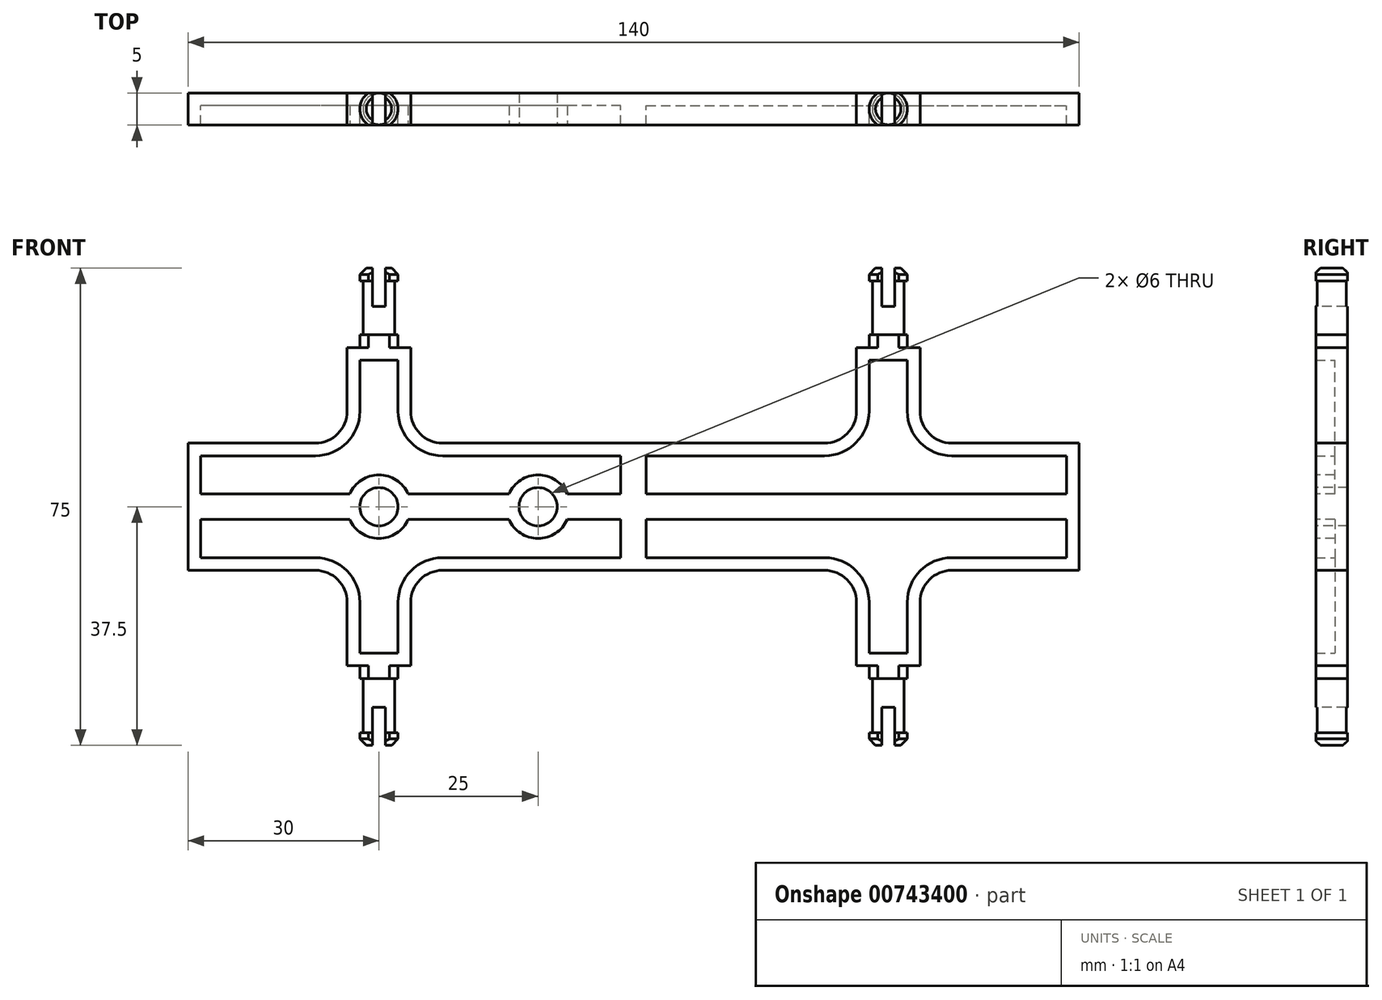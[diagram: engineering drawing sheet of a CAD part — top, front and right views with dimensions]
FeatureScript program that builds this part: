
annotation { "Feature Type Name" : "Feature", "Feature Type Description" : "" }
export const myFeature = defineFeature(function(context is Context, id is Id, definition is map)
    precondition{}
    {
        {
            var Q0;
            Q0=qCreatedBy(makeId("Front.planeOp"),FACE);
            var sketch = newSketch(context, id + "F0", { "sketchPlane" : qUnion([Q0])});
            skLineSegment(sketch, "E0.bottom", {"start": v(0, 0) * mm, "end": v(70, 0) * mm});
            skLineSegment(sketch, "E0.top", {"start": v(0, 10) * mm, "end": v(30, 10) * mm});
            skLineSegment(sketch, "E0.left", {"start": v(0, 0) * mm, "end": v(0, 10) * mm});
            skLineSegment(sketch, "E0.right", {"start": v(70, 0) * mm, "end": v(70, 10) * mm});
            skLineSegment(sketch, "E1.top", {"start": v(35, 25) * mm, "end": v(45, 25) * mm});
            skLineSegment(sketch, "E1.left", {"start": v(35, 15) * mm, "end": v(35, 25) * mm});
            skLineSegment(sketch, "E1.right", {"start": v(45, 15) * mm, "end": v(45, 25) * mm});
            skLineSegment(sketch, "E2.trimOffspring", {"start": v(50, 10) * mm, "end": v(70, 10) * mm});
            skPoint(sketch, "E3.visualSharp", {"position": v(35, 10) * mm});
            skArc(sketch, "E3.filletArc", {"start": v(30, 10) * mm, "mid": v(33.54, 11.46) * mm, "end": v(35, 15) * mm});
            skPoint(sketch, "E4.visualSharp", {"position": v(45, 10) * mm});
            skArc(sketch, "E4.filletArc", {"start": v(45, 15) * mm, "mid": v(46.46, 11.46) * mm, "end": v(50, 10) * mm});
            skSolve(sketch);
        }
        {
            var Q0;
            Q0 = qSketchRegion(id + "F0", true);
            extrude(context, id + "F1", {"entities" : qUnion([Q0]), "endBound" : BoundingType.SYMMETRIC, "depth" : 5 * mm, "offsetDistance" : 25 * mm});
        }
        {
            var Q0;
            Q0=makeQuery(id+"F1.opExtrude","CAP_FACE",FACE,{"disambiguationData":[OSD([sQuery(id+"F0.wireOp",EDGE,"E0.bottom"),sQuery(id+"F0.wireOp",EDGE,"E0.top"),sQuery(id+"F0.wireOp",EDGE,"E0.left"),sQuery(id+"F0.wireOp",EDGE,"E0.right"),sQuery(id+"F0.wireOp",EDGE,"E1.top"),sQuery(id+"F0.wireOp",EDGE,"E1.left"),sQuery(id+"F0.wireOp",EDGE,"E1.right"),sQuery(id+"F0.wireOp",EDGE,"E2.trimOffspring"),sQuery(id+"F0.wireOp",EDGE,"E3.filletArc"),sQuery(id+"F0.wireOp",EDGE,"E4.filletArc")])],"isStart":false});
            shell(context, id + "F2", {"entities" : qUnion([Q0]), "thickness" : 2 * mm});
        }
        {
            var Q0;
            Q0=qCreatedBy(makeId("Front.planeOp"),FACE);
            var sketch = newSketch(context, id + "F3", { "sketchPlane" : qUnion([Q0])});
            skLineSegment(sketch, "E5", {"start": v(40, 25) * mm, "end": v(40, 37.5) * mm});
            skLineSegment(sketch, "E6", {"start": v(40, 37.5) * mm, "end": v(37, 37.5) * mm});
            skLineSegment(sketch, "E7", {"start": v(37, 37.5) * mm, "end": v(37, 35.5) * mm});
            skLineSegment(sketch, "E8", {"start": v(37, 35.5) * mm, "end": v(37.5, 35.5) * mm});
            skLineSegment(sketch, "E9", {"start": v(37.5, 35.5) * mm, "end": v(37.5, 27) * mm});
            skLineSegment(sketch, "E10", {"start": v(37.5, 27) * mm, "end": v(37, 27) * mm});
            skLineSegment(sketch, "E11", {"start": v(37, 27) * mm, "end": v(37, 25) * mm});
            skLineSegment(sketch, "E12", {"start": v(37, 25) * mm, "end": v(40, 25) * mm});
            skSolve(sketch);
        }
        {
            var Q0;
            Q0 = qSketchRegion(id + "F3", true);
            var Q1;
            Q1=sQuery(id+"F3.wireOp",EDGE,"E5");
            revolve(context, id + "F4", {"operationType" : NewBodyOperationType.ADD, "surfaceOperationType" : NewSurfaceOperationType.NEW, "entities" : qUnion([Q0]), "axis" : qUnion([Q1]), "revolveType" : RevolveType.FULL});
        }
        {
            var Q0;
            Q0=makeQuery(id+"F4.opRevolve","SWEPT_FACE",FACE,{"disambiguationData":[OSD([sQuery(id+"F3.wireOp",EDGE,"E6")])]});
            chamfer(context, id + "F5", {"entities" : qUnion([Q0]), "width" : 1 * mm, "tangentPropagation" : true});
        }
        {
            var Q0;
            Q0=makeQuery(id+"F4.opRevolve","SWEPT_FACE",FACE,{"disambiguationData":[OSD([sQuery(id+"F3.wireOp",EDGE,"E6")])]});
            var sketch = newSketch(context, id + "F6", { "sketchPlane" : qUnion([Q0])});
            skLineSegment(sketch, "E13.bottom", {"start": v(0, 2.5) * mm, "end": v(75, 2.5) * mm});
            skLineSegment(sketch, "E13.top", {"start": v(0, -2.5) * mm, "end": v(75, -2.5) * mm});
            skLineSegment(sketch, "E13.left", {"start": v(0, 2.5) * mm, "end": v(0, -2.5) * mm});
            skLineSegment(sketch, "E13.right", {"start": v(75, 2.5) * mm, "end": v(75, -2.5) * mm});
            skSolve(sketch);
        }
        {
            var Q0;
            Q0 = qSketchRegion(id + "F6", true);
            extrude(context, id + "F7", {"entities" : qUnion([Q0]), "operationType" : NewBodyOperationType.INTERSECT, "endBound" : BoundingType.THROUGH_ALL, "oppositeDirection" : true, "depth" : 25 * mm, "offsetDistance" : 25 * mm});
        }
        {
            var Q0;
            Q0=makeQuery(id+"F4.opRevolve","SWEPT_FACE",FACE,{"disambiguationData":[OSD([sQuery(id+"F3.wireOp",EDGE,"E6")])]});
            var sketch = newSketch(context, id + "F8", { "sketchPlane" : qUnion([Q0])});
            skLineSegment(sketch, "E14.bottom", {"start": v(39, 4.04) * mm, "end": v(41, 4.04) * mm});
            skLineSegment(sketch, "E14.top", {"start": v(39, -3.46) * mm, "end": v(41, -3.46) * mm});
            skLineSegment(sketch, "E14.left", {"start": v(39, 4.04) * mm, "end": v(39, -3.46) * mm});
            skLineSegment(sketch, "E14.right", {"start": v(41, 4.04) * mm, "end": v(41, -3.46) * mm});
            skSolve(sketch);
        }
        {
            var Q0;
            Q0 = qSketchRegion(id + "F8", true);
            extrude(context, id + "F9", {"entities" : qUnion([Q0]), "operationType" : NewBodyOperationType.REMOVE, "oppositeDirection" : true, "depth" : 6 * mm, "offsetDistance" : 25 * mm});
        }
        {
            var Q0;
            Q0=makeQuery(id+"F1.opExtrude","SWEPT_BODY",BODY,{"disambiguationData":[OSD([sQuery(id+"F0.wireOp",EDGE,"E0.bottom"),sQuery(id+"F0.wireOp",EDGE,"E0.top"),sQuery(id+"F0.wireOp",EDGE,"E0.left"),sQuery(id+"F0.wireOp",EDGE,"E0.right"),sQuery(id+"F0.wireOp",EDGE,"E1.top"),sQuery(id+"F0.wireOp",EDGE,"E1.left"),sQuery(id+"F0.wireOp",EDGE,"E1.right"),sQuery(id+"F0.wireOp",EDGE,"E2.trimOffspring"),sQuery(id+"F0.wireOp",EDGE,"E3.filletArc"),sQuery(id+"F0.wireOp",EDGE,"E4.filletArc")])]});
            var Q1;
            Q1=qCreatedBy(makeId("Top.planeOp"),FACE);
            mirror(context, id + "F10", {"operationType" : NewBodyOperationType.ADD, "entities" : qUnion([Q0]), "mirrorPlane" : qUnion([Q1])});
        }
        {
            var Q0;
            Q0=makeQuery(id+"F1.opExtrude","SWEPT_BODY",BODY,{"disambiguationData":[OSD([sQuery(id+"F0.wireOp",EDGE,"E0.bottom"),sQuery(id+"F0.wireOp",EDGE,"E0.top"),sQuery(id+"F0.wireOp",EDGE,"E0.left"),sQuery(id+"F0.wireOp",EDGE,"E0.right"),sQuery(id+"F0.wireOp",EDGE,"E1.top"),sQuery(id+"F0.wireOp",EDGE,"E1.left"),sQuery(id+"F0.wireOp",EDGE,"E1.right"),sQuery(id+"F0.wireOp",EDGE,"E2.trimOffspring"),sQuery(id+"F0.wireOp",EDGE,"E3.filletArc"),sQuery(id+"F0.wireOp",EDGE,"E4.filletArc")])]});
            var Q1;
            Q1=qCreatedBy(makeId("Right.planeOp"),FACE);
            mirror(context, id + "F11", {"operationType" : NewBodyOperationType.ADD, "entities" : qUnion([Q0]), "mirrorPlane" : qUnion([Q1])});
        }
        {
            var Q0;
            {var subQ0=makeQuery(id+"F7.boolean.opBoolean","MERGE",FACE,{"derivedFrom":[makeQuery(id+"F1.opExtrude","CAP_FACE",FACE,{"disambiguationData":[OSD([sQuery(id+"F0.wireOp",EDGE,"E0.bottom"),sQuery(id+"F0.wireOp",EDGE,"E0.top"),sQuery(id+"F0.wireOp",EDGE,"E0.left"),sQuery(id+"F0.wireOp",EDGE,"E0.right"),sQuery(id+"F0.wireOp",EDGE,"E1.top"),sQuery(id+"F0.wireOp",EDGE,"E1.left"),sQuery(id+"F0.wireOp",EDGE,"E1.right"),sQuery(id+"F0.wireOp",EDGE,"E2.trimOffspring"),sQuery(id+"F0.wireOp",EDGE,"E3.filletArc"),sQuery(id+"F0.wireOp",EDGE,"E4.filletArc")])],"isStart":false}),makeQuery(id+"F7.boolean.toolComplement.opBoolean","COPY",FACE,{"derivedFrom":makeQuery(id+"F7.opExtrude","SWEPT_FACE",FACE,{"disambiguationData":[OSD([sQuery(id+"F6.wireOp",EDGE,"E13.top")])]})})]});var subQ1=makeQuery(id+"F10.boolean.opBoolean","MERGE",FACE,{"derivedFrom":[subQ0,makeQuery(id+"F10.opPattern","COPY",FACE,{"derivedFrom":subQ0,"instanceName":"1"})]});Q0=makeQuery(id+"F11.boolean.opBoolean","MERGE",FACE,{"derivedFrom":[subQ1,makeQuery(id+"F11.opPattern","COPY",FACE,{"derivedFrom":subQ1,"instanceName":"1"})]});}
            var sketch = newSketch(context, id + "F12", { "sketchPlane" : qUnion([Q0])});
            skCircle(sketch, "E15", {"center": v(-40, 0) * mm, "radius": 5 * mm});
            skCircle(sketch, "E16", {"center": v(-15, 0) * mm, "radius": 5 * mm});
            skSolve(sketch);
        }
        {
            var Q0;
            Q0 = qSketchRegion(id + "F12", true);
            extrude(context, id + "F13", {"entities" : qUnion([Q0]), "operationType" : NewBodyOperationType.ADD, "endBound" : BoundingType.UP_TO_NEXT, "oppositeDirection" : true, "depth" : 25 * mm, "offsetDistance" : 25 * mm});
        }
        {
            var Q0;
            {var subQ0=makeQuery(id+"F7.boolean.opBoolean","MERGE",FACE,{"derivedFrom":[makeQuery(id+"F1.opExtrude","CAP_FACE",FACE,{"disambiguationData":[OSD([sQuery(id+"F0.wireOp",EDGE,"E0.bottom"),sQuery(id+"F0.wireOp",EDGE,"E0.top"),sQuery(id+"F0.wireOp",EDGE,"E0.left"),sQuery(id+"F0.wireOp",EDGE,"E0.right"),sQuery(id+"F0.wireOp",EDGE,"E1.top"),sQuery(id+"F0.wireOp",EDGE,"E1.left"),sQuery(id+"F0.wireOp",EDGE,"E1.right"),sQuery(id+"F0.wireOp",EDGE,"E2.trimOffspring"),sQuery(id+"F0.wireOp",EDGE,"E3.filletArc"),sQuery(id+"F0.wireOp",EDGE,"E4.filletArc")])],"isStart":false}),makeQuery(id+"F7.boolean.toolComplement.opBoolean","COPY",FACE,{"derivedFrom":makeQuery(id+"F7.opExtrude","SWEPT_FACE",FACE,{"disambiguationData":[OSD([sQuery(id+"F6.wireOp",EDGE,"E13.top")])]})})]});var subQ1=makeQuery(id+"F10.boolean.opBoolean","MERGE",FACE,{"derivedFrom":[subQ0,makeQuery(id+"F10.opPattern","COPY",FACE,{"derivedFrom":subQ0,"instanceName":"1"})]});Q0=makeQuery(id+"F13.boolean.opBoolean","MERGE",FACE,{"derivedFrom":[makeQuery(id+"F11.boolean.opBoolean","MERGE",FACE,{"derivedFrom":[subQ1,makeQuery(id+"F11.opPattern","COPY",FACE,{"derivedFrom":subQ1,"instanceName":"1"})]}),makeQuery(id+"F13.opExtrude","CAP_FACE",FACE,{"disambiguationData":[OSD([sQuery(id+"F12.wireOp",EDGE,"E15")])],"isStart":true}),makeQuery(id+"F13.opExtrude","CAP_FACE",FACE,{"disambiguationData":[OSD([sQuery(id+"F12.wireOp",EDGE,"E16")])],"isStart":true})]});}
            var sketch = newSketch(context, id + "F14", { "sketchPlane" : qUnion([Q0])});
            skPoint(sketch, "E17", {"position": v(-40, 0) * mm});
            skPoint(sketch, "E18", {"position": v(-15, 0) * mm});
            skSolve(sketch);
        }
        {
            var Q0;
            Q0=sQuery(id+"F14.wireOp",VERTEX,"E17");
            var Q1;
            Q1=sQuery(id+"F14.wireOp",VERTEX,"E18");
            var Q2;
            Q2=makeQuery(id+"F1.opExtrude","SWEPT_BODY",BODY,{"disambiguationData":[OSD([sQuery(id+"F0.wireOp",EDGE,"E0.bottom"),sQuery(id+"F0.wireOp",EDGE,"E0.top"),sQuery(id+"F0.wireOp",EDGE,"E0.left"),sQuery(id+"F0.wireOp",EDGE,"E0.right"),sQuery(id+"F0.wireOp",EDGE,"E1.top"),sQuery(id+"F0.wireOp",EDGE,"E1.left"),sQuery(id+"F0.wireOp",EDGE,"E1.right"),sQuery(id+"F0.wireOp",EDGE,"E2.trimOffspring"),sQuery(id+"F0.wireOp",EDGE,"E3.filletArc"),sQuery(id+"F0.wireOp",EDGE,"E4.filletArc")])]});
            hole(context, id + "F15", {"style" : HoleStyle.SIMPLE, "endStyle" : HoleEndStyle.THROUGH, "holeDiameter" : 6 * mm, "majorDiameter" : 5 * mm, "isTappedThrough" : true, "tappedDepth" : 12 * mm, "tapClearance" : 3, "locations" : qUnion([Q0, Q1]), "scope" : qUnion([Q2])});
        }
    });
